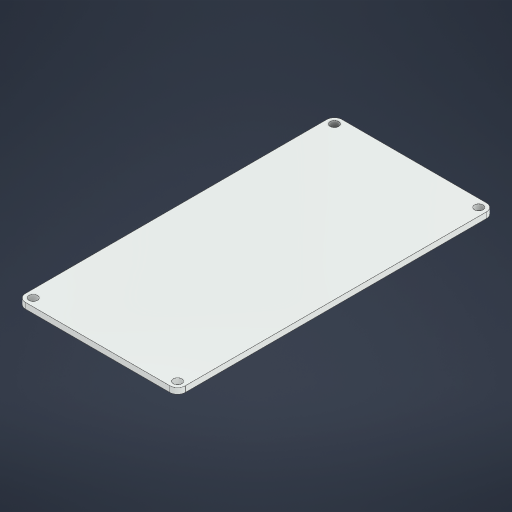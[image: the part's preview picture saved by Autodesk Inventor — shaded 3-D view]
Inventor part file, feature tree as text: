
AUTODESK INVENTOR PART (.ipt)
format: ipt  version: 2024.2 (Build 282272000, 272)  size: 188,928 bytes
history: native  units: mm
features: other x2, extrude x1, sketch x1
ambient origin geometry x8: Origin, YZ Plane, XZ Plane, XY Plane, X Axis, Y Axis, Z Axis, Center Point
bodies: Solid1 (feature_tree)
feature tree (4):
  extrude  "Extrusion1"  Depth=82.0mm
  sketch  "Sketch1"  dims[d0=41.392mm d1=82.0mm d2=2.0mm d3=2.2mm d5=2.006mm d6=2.006mm d7=2.2mm d8=2.006mm d9=2.006mm d10=2.2mm d11=2.006mm d12=2.006mm d13=2.2mm d14=2.006mm d15=2.006mm d16=37.386mm d17=1.5mm d18=0.0mm]
  other  "Finish1"
  other  "Finish2"
